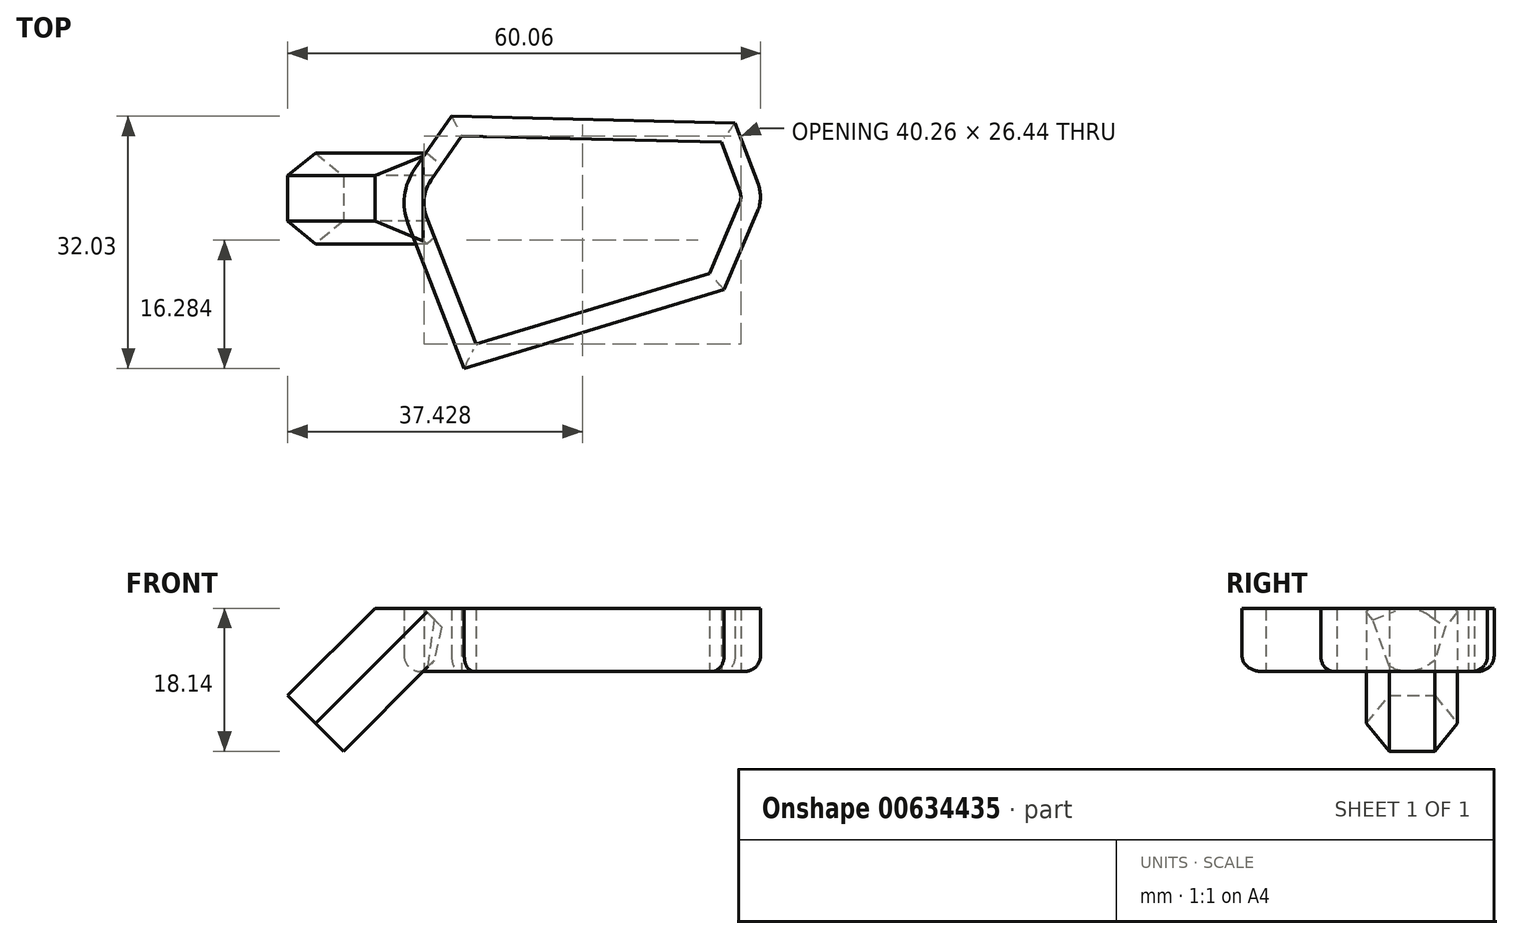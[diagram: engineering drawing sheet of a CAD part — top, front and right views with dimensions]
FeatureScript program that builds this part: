
annotation { "Feature Type Name" : "Feature", "Feature Type Description" : "" }
export const myFeature = defineFeature(function(context is Context, id is Id, definition is map)
    precondition{}
    {
        {
            var Q0;
            Q0=qCreatedBy(makeId("Top.planeOp"),FACE);
            var sketch = newSketch(context, id + "F0", { "sketchPlane" : qUnion([Q0])});
            skLineSegment(sketch, "E0", {"start": v(-12.33, -18.54) * mm, "end": v(17.34, -9.55) * mm});
            skLineSegment(sketch, "E1", {"start": v(-14.15, 7.9) * mm, "end": v(18.84, 7.13) * mm});
            skLineSegment(sketch, "E2", {"start": v(18.84, 7.13) * mm, "end": v(17.34, -9.55) * mm, "construction": true});
            skLineSegment(sketch, "E3", {"start": v(-14.15, 7.9) * mm, "end": v(-12.33, -18.54) * mm, "construction": true});
            skLineSegment(sketch, "E4", {"start": v(-14.15, 7.9) * mm, "end": v(-18.06, 2.3) * mm});
            skLineSegment(sketch, "E5", {"start": v(-18.61, -2.38) * mm, "end": v(-12.33, -18.54) * mm});
            skLineSegment(sketch, "E6", {"start": v(18.84, 7.13) * mm, "end": v(21.18, 0.86) * mm});
            skLineSegment(sketch, "E7", {"start": v(21.15, -0.63) * mm, "end": v(17.34, -9.55) * mm});
            skPoint(sketch, "E8.visualSharp", {"position": v(-19.58, 0.1) * mm});
            skArc(sketch, "E8.filletArc", {"start": v(-18.06, 2.3) * mm, "mid": v(-18.92, 0.03) * mm, "end": v(-18.61, -2.38) * mm});
            skPoint(sketch, "E9.visualSharp", {"position": v(21.46, 0.1) * mm});
            skArc(sketch, "E9.filletArc", {"start": v(21.15, -0.63) * mm, "mid": v(21.3, 0.11) * mm, "end": v(21.18, 0.86) * mm});
            skLineSegment(sketch, "E10.0", {"start": v(-15.43, 10.43) * mm, "end": v(-20.1, 3.72) * mm});
            skArc(sketch, "E10.1", {"start": v(-20.1, 3.72) * mm, "mid": v(-21.4, 0.32) * mm, "end": v(-20.94, -3.28) * mm});
            skLineSegment(sketch, "E10.2", {"start": v(-15.43, 10.43) * mm, "end": v(20.6, 9.6) * mm});
            skLineSegment(sketch, "E10.3", {"start": v(-20.94, -3.28) * mm, "end": v(-13.83, -21.6) * mm});
            skLineSegment(sketch, "E10.4", {"start": v(20.6, 9.6) * mm, "end": v(23.53, 1.73) * mm});
            skArc(sketch, "E10.5", {"start": v(23.45, -1.61) * mm, "mid": v(23.8, 0.05) * mm, "end": v(23.53, 1.73) * mm});
            skLineSegment(sketch, "E10.6", {"start": v(23.45, -1.61) * mm, "end": v(19.18, -11.6) * mm});
            skLineSegment(sketch, "E10.7", {"start": v(-13.83, -21.6) * mm, "end": v(19.18, -11.6) * mm});
            skSolve(sketch);
        }
        {
            var Q0;
            Q0=makeQuery(id+"F0.imprint","IMPRINT",FACE,{"disambiguationData":[TD([[makeQuery(id+"F0.imprint","IMPRINT",EDGE,{"derivedFrom":sQuery(id+"F0.wireOp",EDGE,"E0")}),-1.0]])]});
            extrude(context, id + "F1", {"entities" : qUnion([Q0]), "depth" : 8 * mm, "offsetDistance" : 25 * mm});
        }
        {
            var Q0;
            Q0=makeQuery(id+"F1.opExtrude","CAP_EDGE",EDGE,{"disambiguationData":[OSD([sQuery(id+"F0.wireOp",EDGE,"E10.3")])],"isStart":true});
            var Q1;
            Q1=makeQuery(id+"F1.opExtrude","CAP_EDGE",EDGE,{"disambiguationData":[OSD([sQuery(id+"F0.wireOp",EDGE,"E10.7")])],"isStart":true});
            var Q2;
            Q2=makeQuery(id+"F1.opExtrude","CAP_EDGE",EDGE,{"disambiguationData":[OSD([sQuery(id+"F0.wireOp",EDGE,"E10.6")])],"isStart":true});
            var Q3;
            Q3=makeQuery(id+"F1.opExtrude","CAP_EDGE",EDGE,{"disambiguationData":[OSD([sQuery(id+"F0.wireOp",EDGE,"E10.2")])],"isStart":true});
            fillet(context, id + "F2", {"entities" : qUnion([Q0, Q1, Q2, Q3]), "radius" : 2 * mm, "tangentPropagation" : true, "allowEdgeOverflow" : false});
        }
        {
            var Q0;
            Q0=qCreatedBy(makeId("Top.planeOp"),FACE);
            var sketch = newSketch(context, id + "F3", { "sketchPlane" : qUnion([Q0])});
            skCircle(sketch, "E11.cCircle", {"center": v(-13.33, 0) * mm, "radius": 5 * mm, "construction": true});
            skLineSegment(sketch, "E11.0", {"start": v(-8.33, 2.89) * mm, "end": v(-8.33, -2.89) * mm});
            skLineSegment(sketch, "E11.1", {"start": v(-8.33, -2.89) * mm, "end": v(-13.33, -5.77) * mm});
            skLineSegment(sketch, "E11.2", {"start": v(-13.33, -5.77) * mm, "end": v(-18.33, -2.89) * mm});
            skLineSegment(sketch, "E11.3", {"start": v(-18.33, -2.89) * mm, "end": v(-18.33, 2.89) * mm});
            skLineSegment(sketch, "E11.4", {"start": v(-18.33, 2.89) * mm, "end": v(-13.33, 5.77) * mm});
            skLineSegment(sketch, "E11.5", {"start": v(-13.33, 5.77) * mm, "end": v(-8.33, 2.89) * mm});
            skPoint(sketch, "E11.0.midPoint", {"position": v(-8.33, 0) * mm});
            skSolve(sketch);
        }
        {
            var Q0;
            Q0=qSketchRegion(id+"F3",true);
            extrude(context, id + "F4", {"entities" : qUnion([Q0]), "depth" : 4 * mm, "offsetDistance" : 25 * mm, "hasSecondDirection" : true, "secondDirectionOppositeDirection" : true, "secondDirectionDepth" : 16 * mm});
        }
        {
            var Q0;
            Q0=makeQuery(id+"F4.opExtrude","SWEPT_BODY",BODY,{"disambiguationData":[OSD([sQuery(id+"F3.wireOp",EDGE,"E11.0"),sQuery(id+"F3.wireOp",EDGE,"E11.1"),sQuery(id+"F3.wireOp",EDGE,"E11.2"),sQuery(id+"F3.wireOp",EDGE,"E11.3"),sQuery(id+"F3.wireOp",EDGE,"E11.4"),sQuery(id+"F3.wireOp",EDGE,"E11.5")])]});
            var Q1;
            Q1=makeQuery(id+"F4.opExtrude","CAP_EDGE",EDGE,{"disambiguationData":[OSD([sQuery(id+"F3.wireOp",EDGE,"E11.0")])],"isStart":false});
            transform(context, id + "F5", {"entities" : qUnion([Q0]), "transformType" : TransformType.ROTATION, "transformAxis" : qUnion([Q1]), "angle" : 45 * degree, "oppositeDirection" : true, "makeCopy" : false});
        }
        {
            var Q0;
            Q0=makeQuery(id+"F4.opExtrude","SWEPT_BODY",BODY,{"disambiguationData":[OSD([sQuery(id+"F3.wireOp",EDGE,"E11.0"),sQuery(id+"F3.wireOp",EDGE,"E11.1"),sQuery(id+"F3.wireOp",EDGE,"E11.2"),sQuery(id+"F3.wireOp",EDGE,"E11.3"),sQuery(id+"F3.wireOp",EDGE,"E11.4"),sQuery(id+"F3.wireOp",EDGE,"E11.5")])]});
            transform(context, id + "F6", {"entities" : qUnion([Q0]), "transformType" : TransformType.TRANSLATION_3D, "dx" : -6.7 * mm, "dy" : 0 * mm, "dz" : 0 * mm, "makeCopy" : false});
        }
        {
            var Q0;
            Q0=makeQuery(id+"F0.imprint","IMPRINT",FACE,{"disambiguationData":[TD([[makeQuery(id+"F0.imprint","IMPRINT",EDGE,{"derivedFrom":sQuery(id+"F0.wireOp",EDGE,"E0")}),1.0]])]});
            extrude(context, id + "F7", {"entities" : qUnion([Q0]), "operationType" : NewBodyOperationType.REMOVE, "depth" : 10 * mm, "offsetDistance" : 25 * mm, "hasSecondDirection" : true, "secondDirectionOppositeDirection" : true, "secondDirectionDepth" : 4 * mm});
        }
        {
            var Q0;
            Q0=makeQuery(id+"F1.opExtrude","CAP_FACE",FACE,{"disambiguationData":[OSD([sQuery(id+"F0.wireOp",EDGE,"E0"),sQuery(id+"F0.wireOp",EDGE,"E1"),sQuery(id+"F0.wireOp",EDGE,"E4"),sQuery(id+"F0.wireOp",EDGE,"E5"),sQuery(id+"F0.wireOp",EDGE,"E6"),sQuery(id+"F0.wireOp",EDGE,"E7"),sQuery(id+"F0.wireOp",EDGE,"E8.filletArc"),sQuery(id+"F0.wireOp",EDGE,"E9.filletArc"),sQuery(id+"F0.wireOp",EDGE,"50cba6dd-6752-4126-822d-34af97ffccdd.0"),sQuery(id+"F0.wireOp",EDGE,"50cba6dd-6752-4126-822d-34af97ffccdd.1"),sQuery(id+"F0.wireOp",EDGE,"50cba6dd-6752-4126-822d-34af97ffccdd.2"),sQuery(id+"F0.wireOp",EDGE,"50cba6dd-6752-4126-822d-34af97ffccdd.3"),sQuery(id+"F0.wireOp",EDGE,"50cba6dd-6752-4126-822d-34af97ffccdd.4"),sQuery(id+"F0.wireOp",EDGE,"50cba6dd-6752-4126-822d-34af97ffccdd.5"),sQuery(id+"F0.wireOp",EDGE,"50cba6dd-6752-4126-822d-34af97ffccdd.6"),sQuery(id+"F0.wireOp",EDGE,"50cba6dd-6752-4126-822d-34af97ffccdd.7")])],"isStart":false});
            var sketch = newSketch(context, id + "F8", { "sketchPlane" : qUnion([Q0])});
            skLineSegment(sketch, "E12.bottom", {"start": v(-34.7, 11.94) * mm, "end": v(-8.78, 11.94) * mm});
            skLineSegment(sketch, "E12.top", {"start": v(-34.7, -9.89) * mm, "end": v(-8.78, -9.89) * mm});
            skLineSegment(sketch, "E12.left", {"start": v(-34.7, 11.94) * mm, "end": v(-34.7, -9.89) * mm});
            skLineSegment(sketch, "E12.right", {"start": v(-8.78, 11.94) * mm, "end": v(-8.78, -9.89) * mm});
            skSolve(sketch);
        }
        {
            var Q0;
            Q0=qSketchRegion(id+"F8",true);
            extrude(context, id + "F9", {"entities" : qUnion([Q0]), "operationType" : NewBodyOperationType.REMOVE, "depth" : 25 * mm, "offsetDistance" : 25 * mm});
        }
    });
